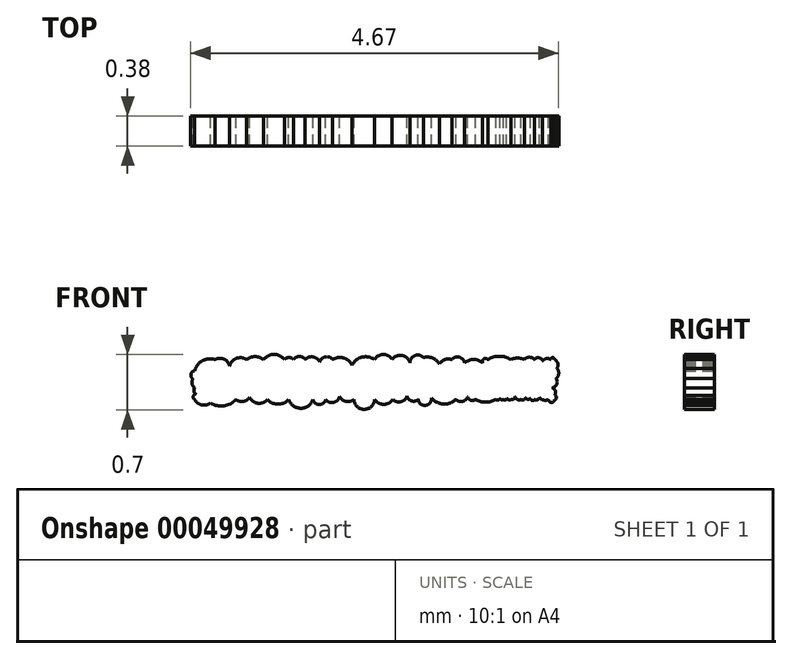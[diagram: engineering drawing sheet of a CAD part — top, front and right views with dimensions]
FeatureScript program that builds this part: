
annotation { "Feature Type Name" : "Feature", "Feature Type Description" : "" }
export const myFeature = defineFeature(function(context is Context, id is Id, definition is map)
    precondition{}
    {
        {
            var Q0;
            Q0=qCreatedBy(makeId("Front.planeOp"),FACE);
            var sketch = newSketch(context, id + "F0", { "sketchPlane" : qUnion([Q0])});
            skLineSegment(sketch, "E0", {"start": v(0, 0) * mm, "end": v(4.57, 0) * mm, "construction": true});
            skLineSegment(sketch, "E1", {"start": v(4.57, 0) * mm, "end": v(4.57, 0.5) * mm, "construction": true});
            skLineSegment(sketch, "E2", {"start": v(4.57, 0.5) * mm, "end": v(0, 0.5) * mm, "construction": true});
            skLineSegment(sketch, "E3", {"start": v(0, 0.5) * mm, "end": v(0, 0) * mm, "construction": true});
            skArc(sketch, "E4", {"start": v(0.26, 0.5) * mm, "mid": v(0.1, 0.5) * mm, "end": v(0, 0.36) * mm});
            skArc(sketch, "E5", {"start": v(0.43, 0.33) * mm, "mid": v(0.41, 0.49) * mm, "end": v(0.26, 0.5) * mm});
            skArc(sketch, "E6", {"start": v(0.66, 0.5) * mm, "mid": v(0.53, 0.52) * mm, "end": v(0.44, 0.43) * mm});
            skArc(sketch, "E7", {"start": v(0.95, 0.4) * mm, "mid": v(0.83, 0.53) * mm, "end": v(0.66, 0.5) * mm});
            skArc(sketch, "E8", {"start": v(1.14, 0.5) * mm, "mid": v(1, 0.57) * mm, "end": v(0.88, 0.5) * mm});
            skArc(sketch, "E9", {"start": v(1.26, 0.4) * mm, "mid": v(1.25, 0.51) * mm, "end": v(1.14, 0.5) * mm});
            skArc(sketch, "E10", {"start": v(1.4, 0.5) * mm, "mid": v(1.33, 0.55) * mm, "end": v(1.26, 0.5) * mm});
            skArc(sketch, "E11", {"start": v(1.6, 0.43) * mm, "mid": v(1.53, 0.54) * mm, "end": v(1.4, 0.5) * mm});
            skArc(sketch, "E12", {"start": v(1.75, 0.5) * mm, "mid": v(1.66, 0.54) * mm, "end": v(1.59, 0.47) * mm});
            skArc(sketch, "E13", {"start": v(2.01, 0.4) * mm, "mid": v(1.91, 0.52) * mm, "end": v(1.75, 0.5) * mm});
            skArc(sketch, "E14", {"start": v(2.29, 0.5) * mm, "mid": v(2.13, 0.54) * mm, "end": v(2, 0.44) * mm});
            skArc(sketch, "E15", {"start": v(0, 0.36) * mm, "mid": v(-0.05, 0.3) * mm, "end": v(0, 0.25) * mm});
            skArc(sketch, "E16", {"start": v(-0.02, 0.26) * mm, "mid": v(-0.03, 0.2) * mm, "end": v(0, 0.15) * mm});
            skArc(sketch, "E17", {"start": v(0, 0.15) * mm, "mid": v(0, 0.08) * mm, "end": v(0.08, 0.08) * mm});
            skArc(sketch, "E18", {"start": v(0.02, 0.07) * mm, "mid": v(-0.02, 0.04) * mm, "end": v(0, 0) * mm});
            skArc(sketch, "E19", {"start": v(0, 0) * mm, "mid": v(0.12, -0.07) * mm, "end": v(0.24, 0) * mm});
            skArc(sketch, "E20", {"start": v(2.5, 0.5) * mm, "mid": v(2.4, 0.57) * mm, "end": v(2.29, 0.5) * mm});
            skArc(sketch, "E21", {"start": v(2.74, 0.43) * mm, "mid": v(2.65, 0.55) * mm, "end": v(2.5, 0.5) * mm});
            skArc(sketch, "E22", {"start": v(2.9, 0.53) * mm, "mid": v(2.8, 0.56) * mm, "end": v(2.74, 0.47) * mm});
            skArc(sketch, "E23", {"start": v(3.1, 0.45) * mm, "mid": v(3.02, 0.53) * mm, "end": v(2.9, 0.53) * mm});
            skArc(sketch, "E24", {"start": v(3.27, 0.5) * mm, "mid": v(3.18, 0.5) * mm, "end": v(3.1, 0.45) * mm});
            skArc(sketch, "E25", {"start": v(3.43, 0.47) * mm, "mid": v(3.36, 0.54) * mm, "end": v(3.27, 0.5) * mm});
            skArc(sketch, "E26", {"start": v(3.66, 0.47) * mm, "mid": v(3.54, 0.5) * mm, "end": v(3.43, 0.47) * mm});
            skArc(sketch, "E27", {"start": v(3.72, 0.5) * mm, "mid": v(3.67, 0.52) * mm, "end": v(3.66, 0.47) * mm});
            skArc(sketch, "E28", {"start": v(4.02, 0.5) * mm, "mid": v(3.87, 0.55) * mm, "end": v(3.72, 0.5) * mm});
            skArc(sketch, "E29", {"start": v(4.26, 0.45) * mm, "mid": v(4.15, 0.52) * mm, "end": v(4.02, 0.5) * mm});
            skArc(sketch, "E30", {"start": v(4.32, 0.5) * mm, "mid": v(4.25, 0.54) * mm, "end": v(4.19, 0.5) * mm});
            skArc(sketch, "E31", {"start": v(4.42, 0.46) * mm, "mid": v(4.39, 0.53) * mm, "end": v(4.32, 0.5) * mm});
            skArc(sketch, "E32", {"start": v(4.52, 0.5) * mm, "mid": v(4.47, 0.52) * mm, "end": v(4.42, 0.49) * mm});
            skArc(sketch, "E33", {"start": v(4.57, 0.5) * mm, "mid": v(4.55, 0.53) * mm, "end": v(4.52, 0.5) * mm});
            skArc(sketch, "E34", {"start": v(4.57, 0.37) * mm, "mid": v(4.62, 0.44) * mm, "end": v(4.57, 0.5) * mm});
            skArc(sketch, "E35", {"start": v(4.57, 0.25) * mm, "mid": v(4.62, 0.32) * mm, "end": v(4.6, 0.4) * mm});
            skArc(sketch, "E36", {"start": v(4.5, 0.15) * mm, "mid": v(4.59, 0.18) * mm, "end": v(4.6, 0.27) * mm});
            skArc(sketch, "E37", {"start": v(4.57, 0.05) * mm, "mid": v(4.58, 0.1) * mm, "end": v(4.54, 0.15) * mm});
            skArc(sketch, "E38", {"start": v(4.57, 0) * mm, "mid": v(4.6, 0.03) * mm, "end": v(4.57, 0.05) * mm});
            skArc(sketch, "E39", {"start": v(4.5, 0) * mm, "mid": v(4.53, -0.04) * mm, "end": v(4.57, 0) * mm});
            skArc(sketch, "E40", {"start": v(4.37, 0.06) * mm, "mid": v(4.42, 0) * mm, "end": v(4.5, 0) * mm});
            skArc(sketch, "E41", {"start": v(4.32, 0) * mm, "mid": v(4.36, 0) * mm, "end": v(4.38, 0.02) * mm});
            skArc(sketch, "E42", {"start": v(4.26, 0.02) * mm, "mid": v(4.29, -0.01) * mm, "end": v(4.32, 0) * mm});
            skArc(sketch, "E43", {"start": v(4.2, 0.03) * mm, "mid": v(4.23, 0) * mm, "end": v(4.26, 0.02) * mm});
            skArc(sketch, "E44", {"start": v(4.14, 0) * mm, "mid": v(4.18, 0) * mm, "end": v(4.2, 0.03) * mm});
            skArc(sketch, "E45", {"start": v(4.07, 0.04) * mm, "mid": v(4.1, 0) * mm, "end": v(4.14, 0) * mm});
            skArc(sketch, "E46", {"start": v(4.02, 0) * mm, "mid": v(4.05, 0) * mm, "end": v(4.07, 0.04) * mm});
            skArc(sketch, "E47", {"start": v(3.96, 0.03) * mm, "mid": v(3.98, 0) * mm, "end": v(4.02, 0) * mm});
            skArc(sketch, "E48", {"start": v(3.96, 0) * mm, "mid": v(3.96, 0.01) * mm, "end": v(3.96, 0.03) * mm});
            skArc(sketch, "E49", {"start": v(3.92, 0) * mm, "mid": v(3.94, 0) * mm, "end": v(3.96, 0) * mm});
            skArc(sketch, "E50", {"start": v(3.87, 0.02) * mm, "mid": v(3.9, 0) * mm, "end": v(3.92, 0) * mm});
            skArc(sketch, "E51", {"start": v(3.83, 0) * mm, "mid": v(3.85, 0) * mm, "end": v(3.88, 0.01) * mm});
            skArc(sketch, "E52", {"start": v(3.56, 0) * mm, "mid": v(3.7, -0.03) * mm, "end": v(3.83, 0) * mm});
            skArc(sketch, "E53", {"start": v(3.47, 0.04) * mm, "mid": v(3.5, 0) * mm, "end": v(3.56, 0) * mm});
            skArc(sketch, "E54", {"start": v(3.32, 0) * mm, "mid": v(3.4, -0.02) * mm, "end": v(3.47, 0.04) * mm});
            skArc(sketch, "E55", {"start": v(2.02, 0) * mm, "mid": v(2.15, -0.13) * mm, "end": v(2.29, 0) * mm});
            skArc(sketch, "E56", {"start": v(2.29, 0) * mm, "mid": v(2.4, -0.06) * mm, "end": v(2.52, 0) * mm});
            skArc(sketch, "E57", {"start": v(2.52, 0) * mm, "mid": v(2.64, -0.02) * mm, "end": v(2.7, 0.08) * mm});
            skArc(sketch, "E58", {"start": v(2.7, 0.04) * mm, "mid": v(2.76, -0.02) * mm, "end": v(2.84, 0) * mm});
            skArc(sketch, "E59", {"start": v(2.84, 0) * mm, "mid": v(2.96, -0.07) * mm, "end": v(2.99, 0.06) * mm});
            skArc(sketch, "E60", {"start": v(3, 0.02) * mm, "mid": v(3.16, -0.06) * mm, "end": v(3.32, 0) * mm});
            skArc(sketch, "E61", {"start": v(0.2, -0.04) * mm, "mid": v(0.37, -0.08) * mm, "end": v(0.52, 0) * mm});
            skArc(sketch, "E62", {"start": v(0.52, 0) * mm, "mid": v(0.67, 0) * mm, "end": v(0.7, 0.15) * mm});
            skArc(sketch, "E63", {"start": v(0.7, 0.03) * mm, "mid": v(0.8, -0.05) * mm, "end": v(0.92, 0) * mm});
            skArc(sketch, "E64", {"start": v(0.92, 0) * mm, "mid": v(1.11, -0.05) * mm, "end": v(1.24, 0.1) * mm});
            skArc(sketch, "E65", {"start": v(1.2, 0) * mm, "mid": v(1.35, -0.11) * mm, "end": v(1.5, 0) * mm});
            skArc(sketch, "E66", {"start": v(1.5, 0) * mm, "mid": v(1.58, -0.06) * mm, "end": v(1.66, 0) * mm});
            skArc(sketch, "E67", {"start": v(1.66, 0) * mm, "mid": v(1.78, -0.03) * mm, "end": v(1.84, 0.07) * mm});
            skArc(sketch, "E68", {"start": v(1.84, 0.04) * mm, "mid": v(1.92, -0.02) * mm, "end": v(2.02, 0) * mm});
            skSolve(sketch);
        }
        {
            var Q0;
            Q0 = qSketchRegion(id + "F0", true);
            extrude(context, id + "F1", {"entities" : qUnion([Q0]), "depth" : 0.38 * mm});
        }
    });
